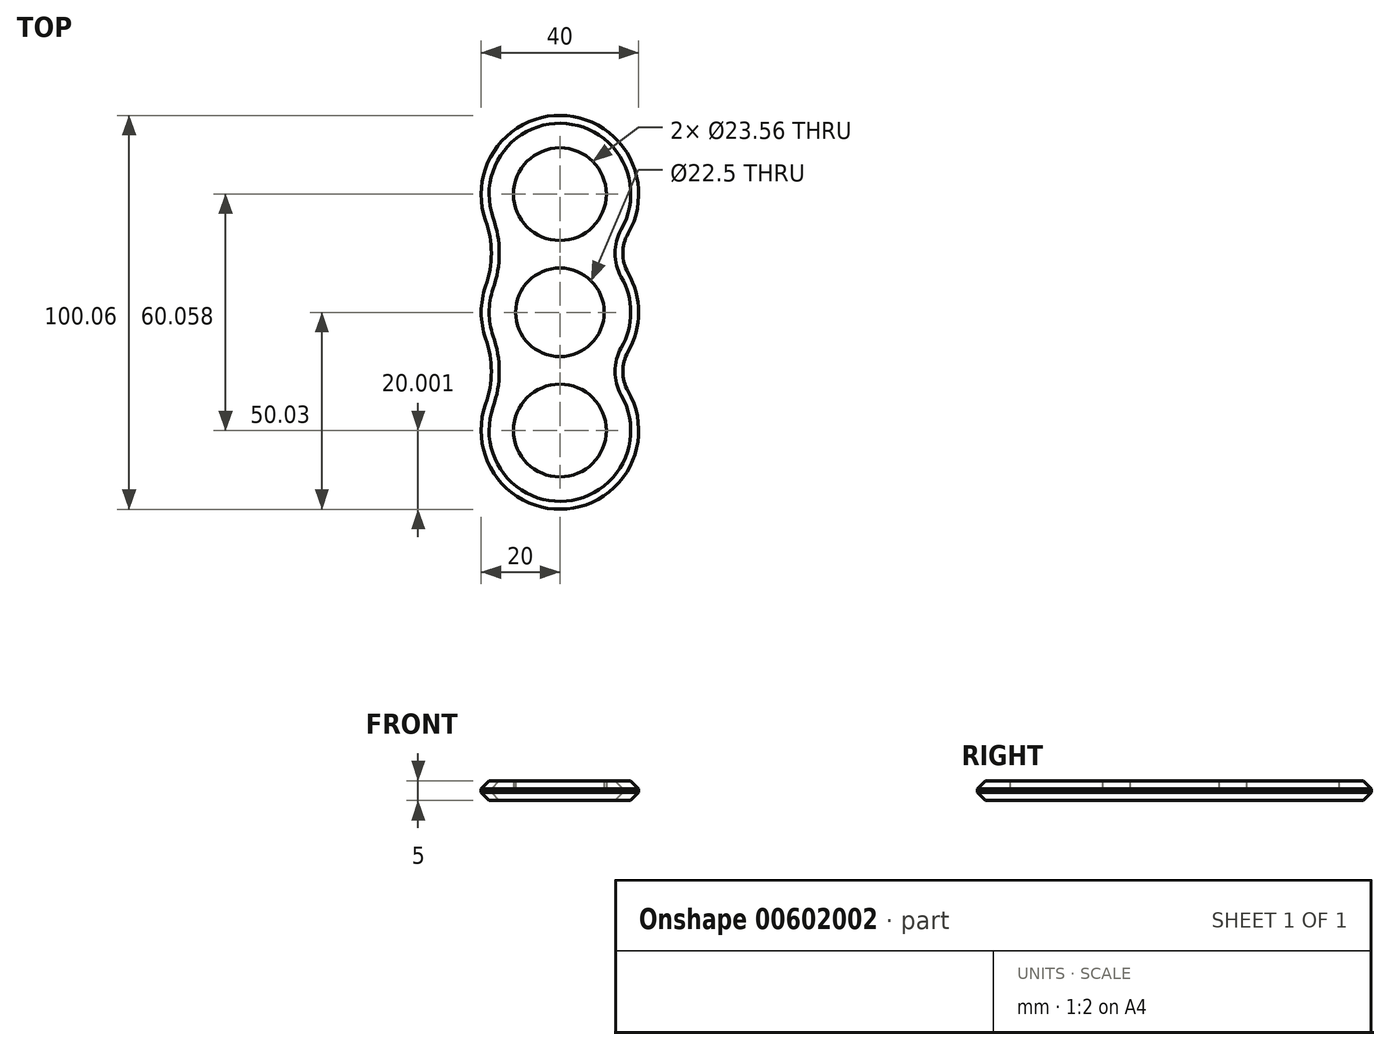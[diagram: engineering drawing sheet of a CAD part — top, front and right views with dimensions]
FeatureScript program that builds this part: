
annotation { "Feature Type Name" : "Feature", "Feature Type Description" : "" }
export const myFeature = defineFeature(function(context is Context, id is Id, definition is map)
    precondition{}
    {
        {
            var Q0;
            Q0=qCreatedBy(makeId("Top.planeOp"),FACE);
            var sketch = newSketch(context, id + "F0", { "sketchPlane" : qUnion([Q0])});
            skCircle(sketch, "E0", {"center": v(0, 0) * mm, "radius": 11.25 * mm});
            skCircle(sketch, "E1", {"center": v(0, 30.03) * mm, "radius": 11.78 * mm});
            skCircle(sketch, "E2.1.0", {"center": v(0, -30.03) * mm, "radius": 11.78 * mm});
            skCircle(sketch, "E3", {"center": v(0, 30.03) * mm, "radius": 20 * mm});
            skCircle(sketch, "E4", {"center": v(0, 0) * mm, "radius": 20 * mm});
            skCircle(sketch, "E5", {"center": v(0, -30.03) * mm, "radius": 20 * mm});
            skSolve(sketch);
        }
        {
            var Q0;
            {var subQ0=sQuery(id+"F0.wireOp",EDGE,"E3");var subQ1=sQuery(id+"F0.wireOp",EDGE,"E0");var subQ2=makeQuery(id+"F0.imprint","INTERSECT",VERTEX,{"disambiguationData":[OD(0.0)],"derivedFrom":[subQ1,subQ0]});Q0=makeQuery(id+"F0.imprint","IMPRINT",FACE,{"disambiguationData":[TD([[makeQuery(id+"F0.imprint","IMPRINT",EDGE,{"disambiguationData":[TD([[subQ2,-1.0]])],"derivedFrom":subQ1}),-1.0]])]});}
            var Q1;
            {var subQ0=sQuery(id+"F0.wireOp",EDGE,"E3");var subQ1=sQuery(id+"F0.wireOp",EDGE,"E0");var subQ2=makeQuery(id+"F0.imprint","INTERSECT",VERTEX,{"disambiguationData":[OD(1.0)],"derivedFrom":[subQ1,subQ0]});Q1=makeQuery(id+"F0.imprint","IMPRINT",FACE,{"disambiguationData":[TD([[makeQuery(id+"F0.imprint","IMPRINT",EDGE,{"disambiguationData":[TD([[subQ2,1.0]])],"derivedFrom":subQ1}),-1.0]])]});}
            var Q2;
            {var subQ1=sQuery(id+"F0.wireOp",EDGE,"E3");var subQ3=sQuery(id+"F0.wireOp",EDGE,"E0");var subQ4=makeQuery(id+"F0.imprint","INTERSECT",VERTEX,{"disambiguationData":[OD(0.0)],"derivedFrom":[subQ3,subQ1]});Q2=makeQuery(id+"F0.imprint","IMPRINT",FACE,{"disambiguationData":[TD([[makeQuery(id+"F0.imprint","IMPRINT",EDGE,{"disambiguationData":[TD([[subQ4,1.0]])],"derivedFrom":subQ3}),-1.0]])]});}
            var Q3;
            {var subQ0=sQuery(id+"F0.wireOp",EDGE,"E5");var subQ7=sQuery(id+"F0.wireOp",EDGE,"E0");var subQ8=makeQuery(id+"F0.imprint","INTERSECT",VERTEX,{"disambiguationData":[OD(0.0)],"derivedFrom":[subQ7,subQ0]});Q3=makeQuery(id+"F0.imprint","IMPRINT",FACE,{"disambiguationData":[TD([[makeQuery(id+"F0.imprint","IMPRINT",EDGE,{"disambiguationData":[TD([[subQ8,-1.0]])],"derivedFrom":subQ7}),-1.0]])]});}
            var Q4;
            {var subQ0=sQuery(id+"F0.wireOp",EDGE,"E4");var subQ1=sQuery(id+"F0.wireOp",EDGE,"E1");var subQ2=makeQuery(id+"F0.imprint","INTERSECT",VERTEX,{"disambiguationData":[OD(0.0)],"derivedFrom":[subQ1,subQ0]});Q4=makeQuery(id+"F0.imprint","IMPRINT",FACE,{"disambiguationData":[TD([[makeQuery(id+"F0.imprint","IMPRINT",EDGE,{"disambiguationData":[TD([[subQ2,-1.0]])],"derivedFrom":subQ1}),-1.0]])]});}
            var Q5;
            {var subQ0=sQuery(id+"F0.wireOp",EDGE,"E4");var subQ1=sQuery(id+"F0.wireOp",EDGE,"E2.1.0");var subQ2=makeQuery(id+"F0.imprint","INTERSECT",VERTEX,{"disambiguationData":[OD(0.0)],"derivedFrom":[subQ1,subQ0]});Q5=makeQuery(id+"F0.imprint","IMPRINT",FACE,{"disambiguationData":[TD([[makeQuery(id+"F0.imprint","IMPRINT",EDGE,{"disambiguationData":[TD([[subQ2,-1.0]])],"derivedFrom":subQ1}),-1.0]])]});}
            extrude(context, id + "F1", {"entities" : qUnion([Q0, Q1, Q2, Q3, Q4, Q5]), "depth" : 5 * mm, "offsetDistance" : 25 * mm});
        }
        {
            var Q0;
            {var subQ0=sQuery(id+"F0.wireOp",EDGE,"E5");var subQ1=sQuery(id+"F0.wireOp",EDGE,"E4");Q0=makeQuery(id+"F1.opExtrude","SWEPT_EDGE",EDGE,{"disambiguationData":[OSD([subQ1,subQ0]),TDD([makeQuery(id+"F0.imprint","INTERSECT",VERTEX,{"disambiguationData":[OD(1.0)],"derivedFrom":[subQ1,subQ0]})])]});}
            var Q1;
            {var subQ0=sQuery(id+"F0.wireOp",EDGE,"E4");var subQ1=sQuery(id+"F0.wireOp",EDGE,"E3");Q1=makeQuery(id+"F1.opExtrude","SWEPT_EDGE",EDGE,{"disambiguationData":[OSD([subQ1,subQ0]),TDD([makeQuery(id+"F0.imprint","INTERSECT",VERTEX,{"disambiguationData":[OD(1.0)],"derivedFrom":[subQ1,subQ0]})])]});}
            fillet(context, id + "F2", {"entities" : qUnion([Q0, Q1]), "radius" : 10 * mm, "tangentPropagation" : true, "allowEdgeOverflow" : false});
        }
        {
            var Q0;
            {var subQ0=sQuery(id+"F0.wireOp",EDGE,"E5");var subQ1=sQuery(id+"F0.wireOp",EDGE,"E4");Q0=makeQuery(id+"F1.opExtrude","SWEPT_EDGE",EDGE,{"disambiguationData":[OSD([subQ1,subQ0]),TDD([makeQuery(id+"F0.imprint","INTERSECT",VERTEX,{"disambiguationData":[OD(0.0)],"derivedFrom":[subQ1,subQ0]})])]});}
            var Q1;
            {var subQ0=sQuery(id+"F0.wireOp",EDGE,"E4");var subQ1=sQuery(id+"F0.wireOp",EDGE,"E3");Q1=makeQuery(id+"F1.opExtrude","SWEPT_EDGE",EDGE,{"disambiguationData":[OSD([subQ1,subQ0]),TDD([makeQuery(id+"F0.imprint","INTERSECT",VERTEX,{"disambiguationData":[OD(0.0)],"derivedFrom":[subQ1,subQ0]})])]});}
            fillet(context, id + "F3", {"entities" : qUnion([Q0, Q1]), "radius" : 25 * mm, "tangentPropagation" : true, "allowEdgeOverflow" : false});
        }
        {
            var Q0;
            Q0=makeQuery(id+"F1.opExtrude","CAP_EDGE",EDGE,{"disambiguationData":[OSD([sQuery(id+"F0.wireOp",EDGE,"E5")])],"isStart":false});
            var Q1;
            {var subQ0=sQuery(id+"F0.wireOp",EDGE,"E5");var subQ1=sQuery(id+"F0.wireOp",EDGE,"E4");Q1=makeQuery(id+"F3.opFillet","BLEND_EDGE",EDGE,{"blendedFrom":[makeQuery(id+"F1.opExtrude","SWEPT_EDGE",EDGE,{"disambiguationData":[OSD([subQ1,subQ0]),TDD([makeQuery(id+"F0.imprint","INTERSECT",VERTEX,{"disambiguationData":[OD(0.0)],"derivedFrom":[subQ1,subQ0]})])]}),makeQuery(id+"F1.opExtrude","CAP_FACE",FACE,{"disambiguationData":[OSD([sQuery(id+"F0.wireOp",EDGE,"E0"),sQuery(id+"F0.wireOp",EDGE,"E1"),sQuery(id+"F0.wireOp",EDGE,"E2.1.0"),sQuery(id+"F0.wireOp",EDGE,"E3"),subQ1,subQ0])],"isStart":false})],"blendedInto":[makeQuery(id+"F1.opExtrude","CAP_FACE",FACE,{"disambiguationData":[OSD([sQuery(id+"F0.wireOp",EDGE,"E0"),sQuery(id+"F0.wireOp",EDGE,"E1"),sQuery(id+"F0.wireOp",EDGE,"E2.1.0"),sQuery(id+"F0.wireOp",EDGE,"E3"),subQ1,subQ0])],"isStart":false})]});}
            var Q2;
            {var subQ0=sQuery(id+"F0.wireOp",EDGE,"E4");Q2=makeQuery(id+"F1.opExtrude","CAP_EDGE",EDGE,{"disambiguationData":[OSD([subQ0]),TDD([makeQuery(id+"F0.imprint","IMPRINT",EDGE,{"disambiguationData":[TD([[makeQuery(id+"F0.imprint","INTERSECT",VERTEX,{"disambiguationData":[OD(0.0)],"derivedFrom":[sQuery(id+"F0.wireOp",EDGE,"E3"),subQ0]}),-1.0]])],"derivedFrom":subQ0})])],"isStart":false});}
            var Q3;
            {var subQ0=sQuery(id+"F0.wireOp",EDGE,"E4");var subQ1=sQuery(id+"F0.wireOp",EDGE,"E3");Q3=makeQuery(id+"F3.opFillet","BLEND_EDGE",EDGE,{"blendedFrom":[makeQuery(id+"F1.opExtrude","SWEPT_EDGE",EDGE,{"disambiguationData":[OSD([subQ1,subQ0]),TDD([makeQuery(id+"F0.imprint","INTERSECT",VERTEX,{"disambiguationData":[OD(0.0)],"derivedFrom":[subQ1,subQ0]})])]}),makeQuery(id+"F1.opExtrude","CAP_FACE",FACE,{"disambiguationData":[OSD([sQuery(id+"F0.wireOp",EDGE,"E0"),sQuery(id+"F0.wireOp",EDGE,"E1"),sQuery(id+"F0.wireOp",EDGE,"E2.1.0"),subQ1,subQ0,sQuery(id+"F0.wireOp",EDGE,"E5")])],"isStart":false})],"blendedInto":[makeQuery(id+"F1.opExtrude","CAP_FACE",FACE,{"disambiguationData":[OSD([sQuery(id+"F0.wireOp",EDGE,"E0"),sQuery(id+"F0.wireOp",EDGE,"E1"),sQuery(id+"F0.wireOp",EDGE,"E2.1.0"),subQ1,subQ0,sQuery(id+"F0.wireOp",EDGE,"E5")])],"isStart":false})]});}
            var Q4;
            Q4=makeQuery(id+"F1.opExtrude","CAP_EDGE",EDGE,{"disambiguationData":[OSD([sQuery(id+"F0.wireOp",EDGE,"E3")])],"isStart":false});
            var Q5;
            {var subQ0=sQuery(id+"F0.wireOp",EDGE,"E5");var subQ1=sQuery(id+"F0.wireOp",EDGE,"E4");Q5=makeQuery(id+"F2.opFillet","BLEND_EDGE",EDGE,{"blendedFrom":[makeQuery(id+"F1.opExtrude","SWEPT_EDGE",EDGE,{"disambiguationData":[OSD([subQ1,subQ0]),TDD([makeQuery(id+"F0.imprint","INTERSECT",VERTEX,{"disambiguationData":[OD(1.0)],"derivedFrom":[subQ1,subQ0]})])]}),makeQuery(id+"F1.opExtrude","CAP_FACE",FACE,{"disambiguationData":[OSD([sQuery(id+"F0.wireOp",EDGE,"E0"),sQuery(id+"F0.wireOp",EDGE,"E1"),sQuery(id+"F0.wireOp",EDGE,"E2.1.0"),sQuery(id+"F0.wireOp",EDGE,"E3"),subQ1,subQ0])],"isStart":false})],"blendedInto":[makeQuery(id+"F1.opExtrude","CAP_FACE",FACE,{"disambiguationData":[OSD([sQuery(id+"F0.wireOp",EDGE,"E0"),sQuery(id+"F0.wireOp",EDGE,"E1"),sQuery(id+"F0.wireOp",EDGE,"E2.1.0"),sQuery(id+"F0.wireOp",EDGE,"E3"),subQ1,subQ0])],"isStart":false})]});}
            var Q6;
            {var subQ0=sQuery(id+"F0.wireOp",EDGE,"E4");Q6=makeQuery(id+"F1.opExtrude","CAP_EDGE",EDGE,{"disambiguationData":[OSD([subQ0]),TDD([makeQuery(id+"F0.imprint","IMPRINT",EDGE,{"disambiguationData":[TD([[makeQuery(id+"F0.imprint","INTERSECT",VERTEX,{"disambiguationData":[OD(1.0)],"derivedFrom":[sQuery(id+"F0.wireOp",EDGE,"E3"),subQ0]}),1.0]])],"derivedFrom":subQ0})])],"isStart":false});}
            var Q7;
            {var subQ0=sQuery(id+"F0.wireOp",EDGE,"E4");var subQ1=sQuery(id+"F0.wireOp",EDGE,"E3");Q7=makeQuery(id+"F2.opFillet","BLEND_EDGE",EDGE,{"blendedFrom":[makeQuery(id+"F1.opExtrude","SWEPT_EDGE",EDGE,{"disambiguationData":[OSD([subQ1,subQ0]),TDD([makeQuery(id+"F0.imprint","INTERSECT",VERTEX,{"disambiguationData":[OD(1.0)],"derivedFrom":[subQ1,subQ0]})])]}),makeQuery(id+"F1.opExtrude","CAP_FACE",FACE,{"disambiguationData":[OSD([sQuery(id+"F0.wireOp",EDGE,"E0"),sQuery(id+"F0.wireOp",EDGE,"E1"),sQuery(id+"F0.wireOp",EDGE,"E2.1.0"),subQ1,subQ0,sQuery(id+"F0.wireOp",EDGE,"E5")])],"isStart":false})],"blendedInto":[makeQuery(id+"F1.opExtrude","CAP_FACE",FACE,{"disambiguationData":[OSD([sQuery(id+"F0.wireOp",EDGE,"E0"),sQuery(id+"F0.wireOp",EDGE,"E1"),sQuery(id+"F0.wireOp",EDGE,"E2.1.0"),subQ1,subQ0,sQuery(id+"F0.wireOp",EDGE,"E5")])],"isStart":false})]});}
            chamfer(context, id + "F4", {"entities" : qUnion([Q0, Q1, Q2, Q3, Q4, Q5, Q6, Q7]), "width" : 2 * mm, "tangentPropagation" : true});
        }
        {
            var Q0;
            Q0=makeQuery(id+"F1.opExtrude","CAP_EDGE",EDGE,{"disambiguationData":[OSD([sQuery(id+"F0.wireOp",EDGE,"E5")])],"isStart":true});
            chamfer(context, id + "F5", {"entities" : qUnion([Q0]), "width" : 2 * mm, "tangentPropagation" : true});
        }
    });
